# Revit family: Camera-Security-Panasonic-FixedDome-Outdoor-MultiSensor-4xFHD-Vandal_Resistant-Weatherproof-Network-X8570NSeriesX
name_source: partatom
category: Security Devices
revit_build: Autodesk Revit 2016 (Build: 20150714_1515(x64)
units: mm (PartAtom-declared; Revit-internal decimal feet)

## family parameters
Cut with Voids When Loaded = No
Host = Face
Maintain Annotation Orientation = No
OmniClass Number = 23.85.10.14.11
OmniClass Title = Cameras
Part Type = Normal
Room Calculation Point = No
Round Connector Dimension = Use Diameter
Shared = No

## types (2) — shared parameters
C1 to C3 Tilting Range = +30 to +80
C123 Tilt Max = 80.00°
C123 Tilt Min = 30.00°
C123 VV Horizontal Offset = 0.772 "
C123 VV Origin Height = 4.425 "
C123 VV Viewpoint Depth = 2.035 "
C1234 Pan Max = 360.00°
C1234 Pan Min = 0.00°
C1234 Yaw Max = 50.00°
C1234 Yaw Min = -50.00°
C4 Tilt Max = 80.00°
C4 Tilt Min = -15.00°
C4 Tilting Range = -15 to +80
C4 VV Viewpoint Depth = 2.791 "
Camera Pan Angle = 0.00°
Communication Ports = 10Base-T / 100Base-TX / 1000Base-T, RJ45 connector
Date Last Modified = 2018/06/28
Day Or Night = Yes
Diameter = 9.055 "
Equipment Abbreviation = SC
Family Version = 1.0.0
Has POE = Yes
IP Or Analog = IP
Indoor Or Outdoor = Outdoor
Manufacturer = Panasonic
Minimum Illumination = 0 lx
Mobile Terminal Compatibility = iPad / iPhone, AndroidTM mobile terminals
Model Disclaimer = Contact Panasonic for more information
Mounting Positions = Mount Dependent or Surface Mount
Operational Humidity = 10 to 100 % (no condensation)
Operational Temperature = –40 °F to +140 °F
Panning Range for each Sensor = 0 to +360
Product Documentation Link = https://bizpartner.panasonic.net
Product Page URL = https://security.panasonic.com
Provide Feedback = https://www.surveymonkey.com
Regulatory Compliance = UL (UL60950-1), c-UL (CSA C22.2 No.60950-1), CE, IEC60950-1, FCC (Part15 ClassA), ICES003 ClassA, EN55022 ClassB, EN55024
SDXC SDHC SD Memory Card Slot = Yes
Shock Resistance = IK10 (IEC62262)
Storage Temperature = –40 °F to +140 °F
URL = http://security.panasonic.com
Voltage DC = 48 V
Water and Dust Resistance = IP66 (IEC60529), Type 4X (UL50), NEMA 4X compliant
Wide Dynamic Range = Yes
Yawing Range for each Sensor = -50 to +50
z Base Height = 1.417 "
z Camera Pan Axis Length = 3.937 "
z Camera Pan Handle Length = 7.874 "
z Camera Tilt Handle Length = 2.756 "
z Dome Radius = 3.15 "
zero-valued in all types: C4 VV Horizontal Offset, Default Elevation

## per-type parameters (varying)
| type | 169 HFOV Max | 169 HFOV Min | 169 VFOV Max | 169 VFOV Min | 43 HFOV Max | 43 HFOV Min | 43 VFOV Max | 43 VFOV Min | Alarm Input Or Output | Angle Of View | Audio In | Audio Out | Camera Type | Description | Part Description | Power Active |
| WV-S8530N | 99.00° | 53.00° | 54.00° | 30.00° | 81.00° | 44.00° | 60.00° | 33.00° |  | 99 |  |  | 8530 | Security Camera, Dome, Vandal Resistant, Waterproof Network, 4 x Full HD Multi-Sensor, WV-S8530N | Security Camera, Dome, Vandal Resistant, Waterproof Network, 4 x Full HD Multi-Sensor, WV-S8530N | 10.1 W |
| WV-X8570N | 97.00° | 97.00° | 53.00° | 53.00° | 97.00° | 97.00° | 53.00° | 53.00° | ALARM IN 1(Alarm input 1/ Black & white input/ Auto time adjustment input) (x1), ALARM IN 2 (Alarm input 2/ ALARM OUT) (x1), ALARM IN 3 (Alarm input 3/ ALARM OUT/ AUX OUT) (x1) | 97 | Yes | Yes | 8570 | Security Camera, Dome, Vandal Resistant, Waterproof Network, 4 x 4K Ultra HD Multi-Sensor, WV-X8570N | Security Camera, Dome, Vandal Resistant, Waterproof Network, 4 x 4K Ultra HD Multi-Sensor, WV-X8570N | 13.0 W |

note: column(s) folded — value = type name in every type: Model, Part Number

## geometry (parser evidence)
native form markers: Blend x6, Sweep x16
no freeform markers — native parametric forms only
